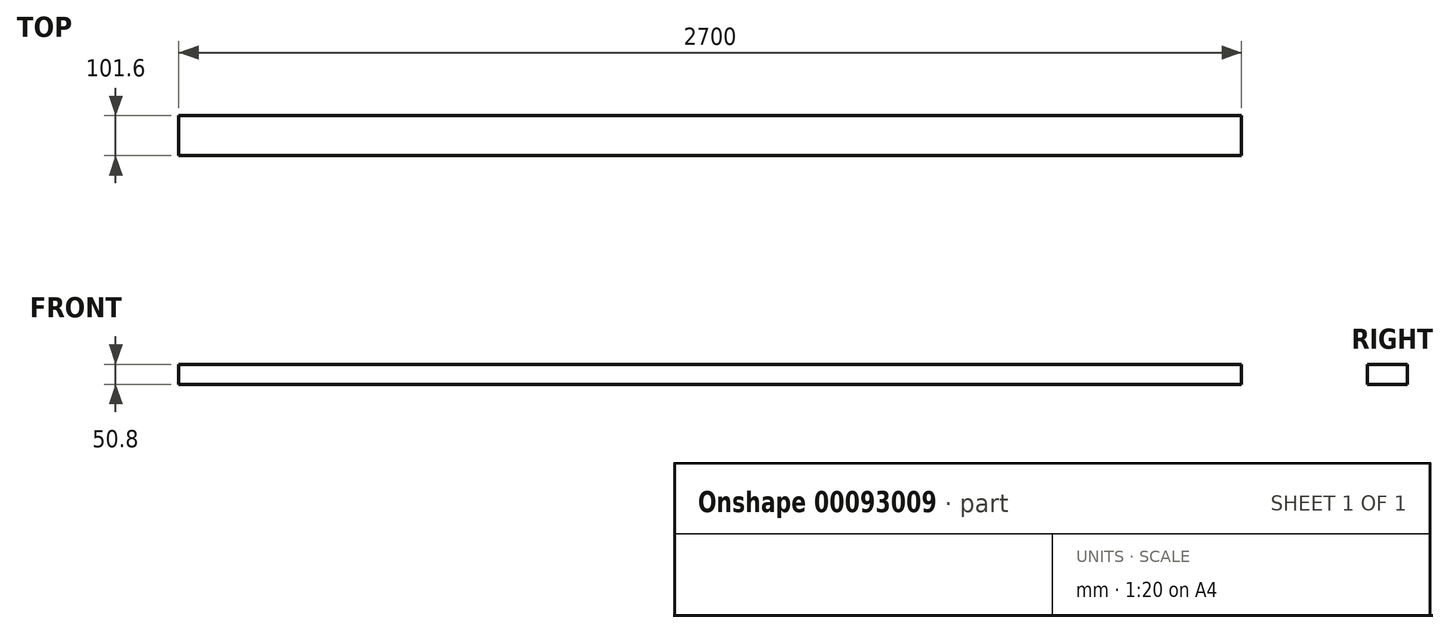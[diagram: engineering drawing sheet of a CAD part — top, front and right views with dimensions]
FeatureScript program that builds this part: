
annotation { "Feature Type Name" : "Feature", "Feature Type Description" : "" }
export const myFeature = defineFeature(function(context is Context, id is Id, definition is map)
    precondition{}
    {
        {
            var Q0;
            Q0=qCreatedBy(makeId("Right.planeOp"),FACE);
            var sketch = newSketch(context, id + "F0", { "sketchPlane" : qUnion([Q0])});
            skLineSegment(sketch, "E0.bottom", {"start": v(-50.8, 25.4) * mm, "end": v(50.8, 25.4) * mm});
            skLineSegment(sketch, "E0.top", {"start": v(-50.8, -25.4) * mm, "end": v(50.8, -25.4) * mm});
            skLineSegment(sketch, "E0.left", {"start": v(-50.8, 25.4) * mm, "end": v(-50.8, -25.4) * mm});
            skLineSegment(sketch, "E0.right", {"start": v(50.8, 25.4) * mm, "end": v(50.8, -25.4) * mm});
            skPoint(sketch, "E0.middle", {"position": v(0, 0) * mm});
            skSolve(sketch);
        }
        {
            var Q0;
            Q0=makeQuery(id+"F0.imprint","IMPRINT",FACE,{"disambiguationData":[TD([[makeQuery(id+"F0.imprint","IMPRINT",EDGE,{"derivedFrom":sQuery(id+"F0.wireOp",EDGE,"E0.bottom")}),-1.0]])]});
            extrude(context, id + "F1", {"entities" : qUnion([Q0]), "endBound" : BoundingType.SYMMETRIC, "depth" : 2700 * mm});
        }
    });
